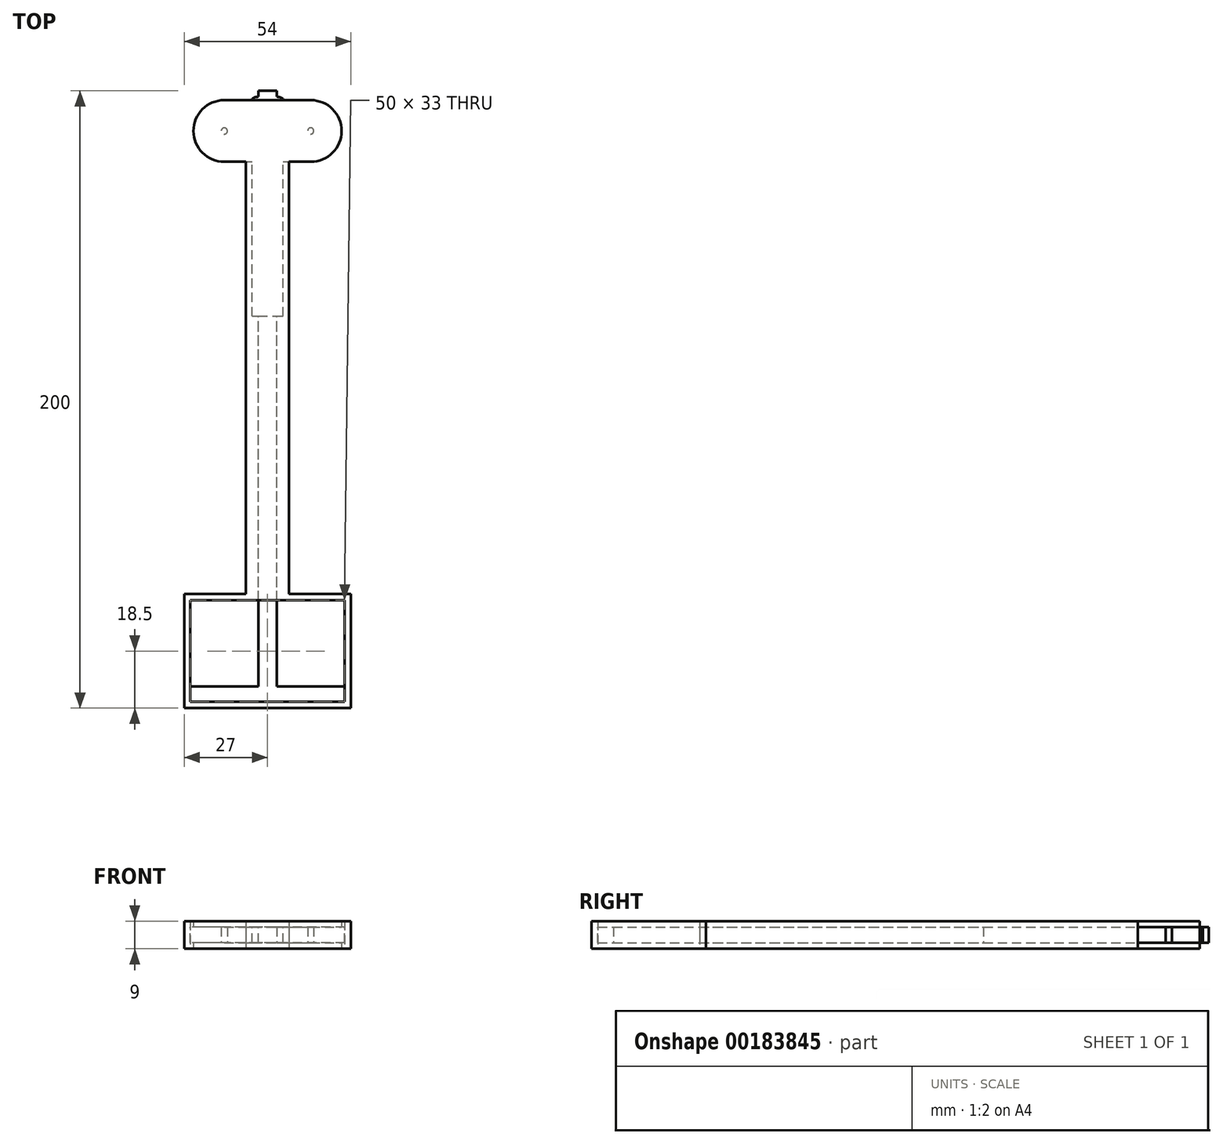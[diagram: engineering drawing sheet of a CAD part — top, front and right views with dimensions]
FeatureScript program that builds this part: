
annotation { "Feature Type Name" : "Feature", "Feature Type Description" : "" }
export const myFeature = defineFeature(function(context is Context, id is Id, definition is map)
    precondition{}
    {
        {
            var Q0;
            Q0=qCreatedBy(makeId("Top.planeOp"),FACE);
            var sketch = newSketch(context, id + "F0", { "sketchPlane" : qUnion([Q0])});
            skLineSegment(sketch, "E0.bottom", {"start": v(0, -180) * mm, "end": v(3, -180) * mm});
            skLineSegment(sketch, "E0.top", {"start": v(0, 13) * mm, "end": v(3, 13) * mm});
            skLineSegment(sketch, "E0.left", {"start": v(0, -180) * mm, "end": v(0, 13) * mm});
            skLineSegment(sketch, "E0.right", {"start": v(3, -180) * mm, "end": v(3, 13) * mm});
            skLineSegment(sketch, "E1", {"start": v(0, 10) * mm, "end": v(3, 10) * mm, "construction": true});
            skArc(sketch, "E2", {"start": v(3, 11.09) * mm, "mid": v(4.04, 10.94) * mm, "end": v(5, 10.5) * mm});
            skLineSegment(sketch, "E3", {"start": v(5, 10.5) * mm, "end": v(5, 10) * mm});
            skArc(sketch, "E4.MirrorCS", {"start": v(3, 8.91) * mm, "mid": v(4.04, 9.06) * mm, "end": v(5, 9.5) * mm});
            skLineSegment(sketch, "E5.MirrorCS", {"start": v(5, 9.5) * mm, "end": v(5, 10) * mm});
            skArc(sketch, "E6.1.0.0", {"start": v(3, 7.89) * mm, "mid": v(4.04, 7.74) * mm, "end": v(5, 7.3) * mm});
            skLineSegment(sketch, "E6.1.0.1", {"start": v(5, 7.3) * mm, "end": v(5, 6.8) * mm});
            skLineSegment(sketch, "E6.1.0.2", {"start": v(5, 6.3) * mm, "end": v(5, 6.8) * mm});
            skArc(sketch, "E6.1.0.3", {"start": v(3, 5.71) * mm, "mid": v(4.04, 5.86) * mm, "end": v(5, 6.3) * mm});
            skArc(sketch, "E6.2.0.0", {"start": v(3, 4.69) * mm, "mid": v(4.04, 4.54) * mm, "end": v(5, 4.1) * mm});
            skLineSegment(sketch, "E6.2.0.1", {"start": v(5, 4.1) * mm, "end": v(5, 3.6) * mm});
            skLineSegment(sketch, "E6.2.0.2", {"start": v(5, 3.1) * mm, "end": v(5, 3.6) * mm});
            skArc(sketch, "E6.2.0.3", {"start": v(3, 2.51) * mm, "mid": v(4.04, 2.66) * mm, "end": v(5, 3.1) * mm});
            skLineSegment(sketch, "E6.direction1", {"start": v(3, 7.39) * mm, "end": v(3, 4.19) * mm, "construction": true});
            skArc(sketch, "E7.0.3.0", {"start": v(3, 1.49) * mm, "mid": v(4.04, 1.34) * mm, "end": v(5, 0.9) * mm});
            skLineSegment(sketch, "E7.4.3.0", {"start": v(5, 0.9) * mm, "end": v(5, 0.4) * mm});
            skLineSegment(sketch, "E7.7.3.0", {"start": v(5, -0.1) * mm, "end": v(5, 0.4) * mm});
            skArc(sketch, "E7.10.3.0", {"start": v(3, -0.69) * mm, "mid": v(4.04, -0.54) * mm, "end": v(5, -0.1) * mm});
            skArc(sketch, "E7.0.4.0", {"start": v(3, -1.71) * mm, "mid": v(4.04, -1.86) * mm, "end": v(5, -2.3) * mm});
            skLineSegment(sketch, "E7.4.4.0", {"start": v(5, -2.3) * mm, "end": v(5, -2.8) * mm});
            skLineSegment(sketch, "E7.7.4.0", {"start": v(5, -3.3) * mm, "end": v(5, -2.8) * mm});
            skArc(sketch, "E7.10.4.0", {"start": v(3, -3.89) * mm, "mid": v(4.04, -3.74) * mm, "end": v(5, -3.3) * mm});
            skArc(sketch, "E7.0.5.0", {"start": v(3, -4.91) * mm, "mid": v(4.04, -5.06) * mm, "end": v(5, -5.5) * mm});
            skLineSegment(sketch, "E7.4.5.0", {"start": v(5, -5.5) * mm, "end": v(5, -6) * mm});
            skLineSegment(sketch, "E7.7.5.0", {"start": v(5, -6.5) * mm, "end": v(5, -6) * mm});
            skArc(sketch, "E7.10.5.0", {"start": v(3, -7.09) * mm, "mid": v(4.04, -6.94) * mm, "end": v(5, -6.5) * mm});
            skArc(sketch, "E7.0.6.0", {"start": v(3, -8.11) * mm, "mid": v(4.04, -8.26) * mm, "end": v(5, -8.7) * mm});
            skLineSegment(sketch, "E7.4.6.0", {"start": v(5, -8.7) * mm, "end": v(5, -9.2) * mm});
            skLineSegment(sketch, "E7.7.6.0", {"start": v(5, -9.7) * mm, "end": v(5, -9.2) * mm});
            skArc(sketch, "E7.10.6.0", {"start": v(3, -10.29) * mm, "mid": v(4.04, -10.14) * mm, "end": v(5, -9.7) * mm});
            skArc(sketch, "E7.0.7.0", {"start": v(3, -11.31) * mm, "mid": v(4.04, -11.46) * mm, "end": v(5, -11.9) * mm});
            skLineSegment(sketch, "E7.4.7.0", {"start": v(5, -11.9) * mm, "end": v(5, -12.4) * mm});
            skLineSegment(sketch, "E7.7.7.0", {"start": v(5, -12.9) * mm, "end": v(5, -12.4) * mm});
            skArc(sketch, "E7.10.7.0", {"start": v(3, -13.49) * mm, "mid": v(4.04, -13.34) * mm, "end": v(5, -12.9) * mm});
            skArc(sketch, "E7.0.8.0", {"start": v(3, -14.51) * mm, "mid": v(4.04, -14.66) * mm, "end": v(5, -15.1) * mm});
            skLineSegment(sketch, "E7.4.8.0", {"start": v(5, -15.1) * mm, "end": v(5, -15.6) * mm});
            skLineSegment(sketch, "E7.7.8.0", {"start": v(5, -16.1) * mm, "end": v(5, -15.6) * mm});
            skArc(sketch, "E7.10.8.0", {"start": v(3, -16.69) * mm, "mid": v(4.04, -16.54) * mm, "end": v(5, -16.1) * mm});
            skArc(sketch, "E7.0.9.0", {"start": v(3, -17.71) * mm, "mid": v(4.04, -17.86) * mm, "end": v(5, -18.3) * mm});
            skLineSegment(sketch, "E7.4.9.0", {"start": v(5, -18.3) * mm, "end": v(5, -18.8) * mm});
            skLineSegment(sketch, "E7.7.9.0", {"start": v(5, -19.3) * mm, "end": v(5, -18.8) * mm});
            skArc(sketch, "E7.10.9.0", {"start": v(3, -19.89) * mm, "mid": v(4.04, -19.74) * mm, "end": v(5, -19.3) * mm});
            skArc(sketch, "E7.0.10.0", {"start": v(3, -20.91) * mm, "mid": v(4.04, -21.06) * mm, "end": v(5, -21.5) * mm});
            skLineSegment(sketch, "E7.4.10.0", {"start": v(5, -21.5) * mm, "end": v(5, -22) * mm});
            skLineSegment(sketch, "E7.7.10.0", {"start": v(5, -22.5) * mm, "end": v(5, -22) * mm});
            skArc(sketch, "E7.10.10.0", {"start": v(3, -23.09) * mm, "mid": v(4.04, -22.94) * mm, "end": v(5, -22.5) * mm});
            skArc(sketch, "E7.0.11.0", {"start": v(3, -24.11) * mm, "mid": v(4.04, -24.26) * mm, "end": v(5, -24.7) * mm});
            skLineSegment(sketch, "E7.4.11.0", {"start": v(5, -24.7) * mm, "end": v(5, -25.2) * mm});
            skLineSegment(sketch, "E7.7.11.0", {"start": v(5, -25.7) * mm, "end": v(5, -25.2) * mm});
            skArc(sketch, "E7.10.11.0", {"start": v(3, -26.29) * mm, "mid": v(4.04, -26.14) * mm, "end": v(5, -25.7) * mm});
            skArc(sketch, "E7.0.12.0", {"start": v(3, -27.31) * mm, "mid": v(4.04, -27.46) * mm, "end": v(5, -27.9) * mm});
            skLineSegment(sketch, "E7.4.12.0", {"start": v(5, -27.9) * mm, "end": v(5, -28.4) * mm});
            skLineSegment(sketch, "E7.7.12.0", {"start": v(5, -28.9) * mm, "end": v(5, -28.4) * mm});
            skArc(sketch, "E7.10.12.0", {"start": v(3, -29.49) * mm, "mid": v(4.04, -29.34) * mm, "end": v(5, -28.9) * mm});
            skArc(sketch, "E7.0.13.0", {"start": v(3, -30.51) * mm, "mid": v(4.04, -30.66) * mm, "end": v(5, -31.1) * mm});
            skLineSegment(sketch, "E7.4.13.0", {"start": v(5, -31.1) * mm, "end": v(5, -31.6) * mm});
            skLineSegment(sketch, "E7.7.13.0", {"start": v(5, -32.1) * mm, "end": v(5, -31.6) * mm});
            skArc(sketch, "E7.10.13.0", {"start": v(3, -32.69) * mm, "mid": v(4.04, -32.54) * mm, "end": v(5, -32.1) * mm});
            skArc(sketch, "E7.0.14.0", {"start": v(3, -33.71) * mm, "mid": v(4.04, -33.86) * mm, "end": v(5, -34.3) * mm});
            skLineSegment(sketch, "E7.4.14.0", {"start": v(5, -34.3) * mm, "end": v(5, -34.8) * mm});
            skLineSegment(sketch, "E7.7.14.0", {"start": v(5, -35.3) * mm, "end": v(5, -34.8) * mm});
            skArc(sketch, "E7.10.14.0", {"start": v(3, -35.89) * mm, "mid": v(4.04, -35.74) * mm, "end": v(5, -35.3) * mm});
            skArc(sketch, "E7.0.15.0", {"start": v(3, -36.91) * mm, "mid": v(4.04, -37.06) * mm, "end": v(5, -37.5) * mm});
            skLineSegment(sketch, "E7.4.15.0", {"start": v(5, -37.5) * mm, "end": v(5, -38) * mm});
            skLineSegment(sketch, "E7.7.15.0", {"start": v(5, -38.5) * mm, "end": v(5, -38) * mm});
            skArc(sketch, "E7.10.15.0", {"start": v(3, -39.09) * mm, "mid": v(4.04, -38.94) * mm, "end": v(5, -38.5) * mm});
            skSolve(sketch);
        }
        {
            var Q0;
            Q0 = qSketchRegion(id + "F0", true);
            extrude(context, id + "F1", {"entities" : qUnion([Q0]), "depth" : 5 * mm});
        }
        {
            var Q0;
            Q0=makeQuery(id+"F1.opExtrude","SWEPT_BODY",BODY,{"disambiguationData":[OSD([sQuery(id+"F0.wireOp",EDGE,"E0.bottom"),sQuery(id+"F0.wireOp",EDGE,"E0.top"),sQuery(id+"F0.wireOp",EDGE,"E0.left"),sQuery(id+"F0.wireOp",EDGE,"E0.right"),sQuery(id+"F0.wireOp",EDGE,"E2"),sQuery(id+"F0.wireOp",EDGE,"E3"),sQuery(id+"F0.wireOp",EDGE,"E4.MirrorCS"),sQuery(id+"F0.wireOp",EDGE,"E5.MirrorCS"),sQuery(id+"F0.wireOp",EDGE,"E6.1.0.0"),sQuery(id+"F0.wireOp",EDGE,"E6.1.0.1"),sQuery(id+"F0.wireOp",EDGE,"E6.1.0.2"),sQuery(id+"F0.wireOp",EDGE,"E6.1.0.3"),sQuery(id+"F0.wireOp",EDGE,"E6.2.0.0"),sQuery(id+"F0.wireOp",EDGE,"E6.2.0.1"),sQuery(id+"F0.wireOp",EDGE,"E6.2.0.2"),sQuery(id+"F0.wireOp",EDGE,"E6.2.0.3"),sQuery(id+"F0.wireOp",EDGE,"E7.0.3.0"),sQuery(id+"F0.wireOp",EDGE,"E7.4.3.0"),sQuery(id+"F0.wireOp",EDGE,"E7.7.3.0"),sQuery(id+"F0.wireOp",EDGE,"E7.10.3.0"),sQuery(id+"F0.wireOp",EDGE,"E7.0.4.0"),sQuery(id+"F0.wireOp",EDGE,"E7.4.4.0"),sQuery(id+"F0.wireOp",EDGE,"E7.7.4.0"),sQuery(id+"F0.wireOp",EDGE,"E7.10.4.0"),sQuery(id+"F0.wireOp",EDGE,"E7.0.5.0"),sQuery(id+"F0.wireOp",EDGE,"E7.4.5.0"),sQuery(id+"F0.wireOp",EDGE,"E7.7.5.0"),sQuery(id+"F0.wireOp",EDGE,"E7.10.5.0"),sQuery(id+"F0.wireOp",EDGE,"E7.0.6.0"),sQuery(id+"F0.wireOp",EDGE,"E7.4.6.0"),sQuery(id+"F0.wireOp",EDGE,"E7.7.6.0"),sQuery(id+"F0.wireOp",EDGE,"E7.10.6.0"),sQuery(id+"F0.wireOp",EDGE,"E7.0.7.0"),sQuery(id+"F0.wireOp",EDGE,"E7.4.7.0"),sQuery(id+"F0.wireOp",EDGE,"E7.7.7.0"),sQuery(id+"F0.wireOp",EDGE,"E7.10.7.0"),sQuery(id+"F0.wireOp",EDGE,"E7.0.8.0"),sQuery(id+"F0.wireOp",EDGE,"E7.4.8.0"),sQuery(id+"F0.wireOp",EDGE,"E7.7.8.0"),sQuery(id+"F0.wireOp",EDGE,"E7.10.8.0"),sQuery(id+"F0.wireOp",EDGE,"E7.0.9.0"),sQuery(id+"F0.wireOp",EDGE,"E7.4.9.0"),sQuery(id+"F0.wireOp",EDGE,"E7.7.9.0"),sQuery(id+"F0.wireOp",EDGE,"E7.10.9.0"),sQuery(id+"F0.wireOp",EDGE,"E7.0.10.0"),sQuery(id+"F0.wireOp",EDGE,"E7.4.10.0"),sQuery(id+"F0.wireOp",EDGE,"E7.7.10.0"),sQuery(id+"F0.wireOp",EDGE,"E7.10.10.0"),sQuery(id+"F0.wireOp",EDGE,"E7.0.11.0"),sQuery(id+"F0.wireOp",EDGE,"E7.4.11.0"),sQuery(id+"F0.wireOp",EDGE,"E7.7.11.0"),sQuery(id+"F0.wireOp",EDGE,"E7.10.11.0"),sQuery(id+"F0.wireOp",EDGE,"E7.0.12.0"),sQuery(id+"F0.wireOp",EDGE,"E7.4.12.0"),sQuery(id+"F0.wireOp",EDGE,"E7.7.12.0"),sQuery(id+"F0.wireOp",EDGE,"E7.10.12.0"),sQuery(id+"F0.wireOp",EDGE,"E7.0.13.0"),sQuery(id+"F0.wireOp",EDGE,"E7.4.13.0"),sQuery(id+"F0.wireOp",EDGE,"E7.7.13.0"),sQuery(id+"F0.wireOp",EDGE,"E7.10.13.0"),sQuery(id+"F0.wireOp",EDGE,"E7.0.14.0"),sQuery(id+"F0.wireOp",EDGE,"E7.4.14.0"),sQuery(id+"F0.wireOp",EDGE,"E7.7.14.0"),sQuery(id+"F0.wireOp",EDGE,"E7.10.14.0"),sQuery(id+"F0.wireOp",EDGE,"E7.0.15.0"),sQuery(id+"F0.wireOp",EDGE,"E7.4.15.0"),sQuery(id+"F0.wireOp",EDGE,"E7.7.15.0"),sQuery(id+"F0.wireOp",EDGE,"E7.10.15.0")])]});
            var Q1;
            Q1=makeQuery(id+"F1.opExtrude","SWEPT_FACE",FACE,{"disambiguationData":[OSD([sQuery(id+"F0.wireOp",EDGE,"E0.left")])]});
            mirror(context, id + "F2", {"operationType" : NewBodyOperationType.ADD, "entities" : qUnion([Q0]), "mirrorPlane" : qUnion([Q1])});
        }
        {
            var Q0;
            {var subQ0=makeQuery(id+"F1.opExtrude","SWEPT_FACE",FACE,{"disambiguationData":[OSD([sQuery(id+"F0.wireOp",EDGE,"E0.bottom")])]});Q0=makeQuery(id+"F2.boolean.opBoolean","MERGE",FACE,{"derivedFrom":[subQ0,makeQuery(id+"F2.opPattern","COPY",FACE,{"derivedFrom":subQ0,"instanceName":"1"})]});}
            var sketch = newSketch(context, id + "F3", { "sketchPlane" : qUnion([Q0])});
            skLineSegment(sketch, "E8.bottom", {"start": v(25, 0) * mm, "end": v(-25, 0) * mm});
            skLineSegment(sketch, "E8.top", {"start": v(25, 5) * mm, "end": v(-25, 5) * mm});
            skLineSegment(sketch, "E8.left", {"start": v(25, 0) * mm, "end": v(25, 5) * mm});
            skLineSegment(sketch, "E8.right", {"start": v(-25, 0) * mm, "end": v(-25, 5) * mm});
            skPoint(sketch, "E8.middle", {"position": v(0, 2.5) * mm});
            skPoint(sketch, "E8.middle.positionSnap0", {"position": v(-3, 2.5) * mm});
            skPoint(sketch, "E8.middle.positionSnap1", {"position": v(0, 0) * mm});
            skPoint(sketch, "E8.centerSnap0", {"position": v(-3, 2.5) * mm});
            skPoint(sketch, "E8.centerSnap1", {"position": v(0, 0) * mm});
            skSolve(sketch);
        }
        {
            var Q0;
            Q0 = qSketchRegion(id + "F3", true);
            extrude(context, id + "F4", {"entities" : qUnion([Q0]), "operationType" : NewBodyOperationType.ADD, "depth" : 5 * mm});
        }
        {
            var Q0;
            Q0=qCreatedBy(makeId("Top.planeOp"),FACE);
            var sketch = newSketch(context, id + "F5", { "sketchPlane" : qUnion([Q0])});
            skCircle(sketch, "E9", {"center": v(14, 0) * mm, "radius": 10 * mm});
            skLineSegment(sketch, "E10", {"start": v(7, -10) * mm, "end": v(7, -150) * mm});
            skLineSegment(sketch, "E11", {"start": v(7, -150) * mm, "end": v(27, -150) * mm});
            skLineSegment(sketch, "E12", {"start": v(27, -150) * mm, "end": v(27, -187) * mm});
            skLineSegment(sketch, "E13", {"start": v(27, -187) * mm, "end": v(0, -187) * mm});
            skLineSegment(sketch, "E14", {"start": v(0, 10) * mm, "end": v(14, 10) * mm});
            skLineSegment(sketch, "E15", {"start": v(7, -10) * mm, "end": v(14, -10) * mm});
            skLineSegment(sketch, "E16.MirrorCS", {"start": v(0, 10) * mm, "end": v(-14, 10) * mm});
            skLineSegment(sketch, "E17.MirrorCS", {"start": v(-7, -10) * mm, "end": v(-14, -10) * mm});
            skCircle(sketch, "E18.MirrorC", {"center": v(-14, 0) * mm, "radius": 10 * mm});
            skLineSegment(sketch, "E19.MirrorCS", {"start": v(-7, -10) * mm, "end": v(-7, -150) * mm});
            skLineSegment(sketch, "E20.MirrorCS", {"start": v(-7, -150) * mm, "end": v(-27, -150) * mm});
            skLineSegment(sketch, "E21.MirrorCS", {"start": v(-27, -150) * mm, "end": v(-27, -187) * mm});
            skLineSegment(sketch, "E22.MirrorCS", {"start": v(-27, -187) * mm, "end": v(0, -187) * mm});
            skLineSegment(sketch, "E23.bottom", {"start": v(25, -185) * mm, "end": v(-25, -185) * mm});
            skLineSegment(sketch, "E23.top", {"start": v(25, -152) * mm, "end": v(-25, -152) * mm});
            skLineSegment(sketch, "E23.left", {"start": v(25, -185) * mm, "end": v(25, -152) * mm});
            skLineSegment(sketch, "E23.right", {"start": v(-25, -185) * mm, "end": v(-25, -152) * mm});
            skPoint(sketch, "E23.middle", {"position": v(0, -168.5) * mm});
            skSolve(sketch);
        }
        {
            var Q0;
            Q0 = qSketchRegion(id + "F5", true);
            extrude(context, id + "F6", {"entities" : qUnion([Q0]), "depth" : 7 * mm, "hasSecondDirection" : true, "secondDirectionOppositeDirection" : true, "secondDirectionDepth" : 2 * mm});
        }
        {
            var Q0;
            Q0=makeQuery(id+"F1.opExtrude","SWEPT_BODY",BODY,{"disambiguationData":[OSD([sQuery(id+"F0.wireOp",EDGE,"E0.bottom"),sQuery(id+"F0.wireOp",EDGE,"E0.top"),sQuery(id+"F0.wireOp",EDGE,"E0.left"),sQuery(id+"F0.wireOp",EDGE,"E0.right"),sQuery(id+"F0.wireOp",EDGE,"E2"),sQuery(id+"F0.wireOp",EDGE,"E3"),sQuery(id+"F0.wireOp",EDGE,"E4.MirrorCS"),sQuery(id+"F0.wireOp",EDGE,"E5.MirrorCS"),sQuery(id+"F0.wireOp",EDGE,"E6.1.0.0"),sQuery(id+"F0.wireOp",EDGE,"E6.1.0.1"),sQuery(id+"F0.wireOp",EDGE,"E6.1.0.2"),sQuery(id+"F0.wireOp",EDGE,"E6.1.0.3"),sQuery(id+"F0.wireOp",EDGE,"E6.2.0.0"),sQuery(id+"F0.wireOp",EDGE,"E6.2.0.1"),sQuery(id+"F0.wireOp",EDGE,"E6.2.0.2"),sQuery(id+"F0.wireOp",EDGE,"E6.2.0.3"),sQuery(id+"F0.wireOp",EDGE,"E7.0.3.0"),sQuery(id+"F0.wireOp",EDGE,"E7.4.3.0"),sQuery(id+"F0.wireOp",EDGE,"E7.7.3.0"),sQuery(id+"F0.wireOp",EDGE,"E7.10.3.0"),sQuery(id+"F0.wireOp",EDGE,"E7.0.4.0"),sQuery(id+"F0.wireOp",EDGE,"E7.4.4.0"),sQuery(id+"F0.wireOp",EDGE,"E7.7.4.0"),sQuery(id+"F0.wireOp",EDGE,"E7.10.4.0"),sQuery(id+"F0.wireOp",EDGE,"E7.0.5.0"),sQuery(id+"F0.wireOp",EDGE,"E7.4.5.0"),sQuery(id+"F0.wireOp",EDGE,"E7.7.5.0"),sQuery(id+"F0.wireOp",EDGE,"E7.10.5.0"),sQuery(id+"F0.wireOp",EDGE,"E7.0.6.0"),sQuery(id+"F0.wireOp",EDGE,"E7.4.6.0"),sQuery(id+"F0.wireOp",EDGE,"E7.7.6.0"),sQuery(id+"F0.wireOp",EDGE,"E7.10.6.0"),sQuery(id+"F0.wireOp",EDGE,"E7.0.7.0"),sQuery(id+"F0.wireOp",EDGE,"E7.4.7.0"),sQuery(id+"F0.wireOp",EDGE,"E7.7.7.0"),sQuery(id+"F0.wireOp",EDGE,"E7.10.7.0"),sQuery(id+"F0.wireOp",EDGE,"E7.0.8.0"),sQuery(id+"F0.wireOp",EDGE,"E7.4.8.0"),sQuery(id+"F0.wireOp",EDGE,"E7.7.8.0"),sQuery(id+"F0.wireOp",EDGE,"E7.10.8.0"),sQuery(id+"F0.wireOp",EDGE,"E7.0.9.0"),sQuery(id+"F0.wireOp",EDGE,"E7.4.9.0"),sQuery(id+"F0.wireOp",EDGE,"E7.7.9.0"),sQuery(id+"F0.wireOp",EDGE,"E7.10.9.0"),sQuery(id+"F0.wireOp",EDGE,"E7.0.10.0"),sQuery(id+"F0.wireOp",EDGE,"E7.4.10.0"),sQuery(id+"F0.wireOp",EDGE,"E7.7.10.0"),sQuery(id+"F0.wireOp",EDGE,"E7.10.10.0"),sQuery(id+"F0.wireOp",EDGE,"E7.0.11.0"),sQuery(id+"F0.wireOp",EDGE,"E7.4.11.0"),sQuery(id+"F0.wireOp",EDGE,"E7.7.11.0"),sQuery(id+"F0.wireOp",EDGE,"E7.10.11.0"),sQuery(id+"F0.wireOp",EDGE,"E7.0.12.0"),sQuery(id+"F0.wireOp",EDGE,"E7.4.12.0"),sQuery(id+"F0.wireOp",EDGE,"E7.7.12.0"),sQuery(id+"F0.wireOp",EDGE,"E7.10.12.0"),sQuery(id+"F0.wireOp",EDGE,"E7.0.13.0"),sQuery(id+"F0.wireOp",EDGE,"E7.4.13.0"),sQuery(id+"F0.wireOp",EDGE,"E7.7.13.0"),sQuery(id+"F0.wireOp",EDGE,"E7.10.13.0"),sQuery(id+"F0.wireOp",EDGE,"E7.0.14.0"),sQuery(id+"F0.wireOp",EDGE,"E7.4.14.0"),sQuery(id+"F0.wireOp",EDGE,"E7.7.14.0"),sQuery(id+"F0.wireOp",EDGE,"E7.10.14.0"),sQuery(id+"F0.wireOp",EDGE,"E7.0.15.0"),sQuery(id+"F0.wireOp",EDGE,"E7.4.15.0"),sQuery(id+"F0.wireOp",EDGE,"E7.7.15.0"),sQuery(id+"F0.wireOp",EDGE,"E7.10.15.0")])]});
            var Q1;
            Q1=makeQuery(id+"F6.opExtrude","SWEPT_BODY",BODY,{"disambiguationData":[OSD([sQuery(id+"F5.wireOp",EDGE,"E9"),sQuery(id+"F5.wireOp",EDGE,"E10"),sQuery(id+"F5.wireOp",EDGE,"E11"),sQuery(id+"F5.wireOp",EDGE,"E12"),sQuery(id+"F5.wireOp",EDGE,"E13"),sQuery(id+"F5.wireOp",EDGE,"E14"),sQuery(id+"F5.wireOp",EDGE,"E15"),sQuery(id+"F5.wireOp",EDGE,"E16.MirrorCS"),sQuery(id+"F5.wireOp",EDGE,"E17.MirrorCS"),sQuery(id+"F5.wireOp",EDGE,"E18.MirrorC"),sQuery(id+"F5.wireOp",EDGE,"E19.MirrorCS"),sQuery(id+"F5.wireOp",EDGE,"E20.MirrorCS"),sQuery(id+"F5.wireOp",EDGE,"E21.MirrorCS"),sQuery(id+"F5.wireOp",EDGE,"E22.MirrorCS"),sQuery(id+"F5.wireOp",EDGE,"E23.bottom"),sQuery(id+"F5.wireOp",EDGE,"E23.top"),sQuery(id+"F5.wireOp",EDGE,"E23.left"),sQuery(id+"F5.wireOp",EDGE,"E23.right")])]});
            booleanBodies(context, id + "F7", {"operationType" : BooleanOperationType.SUBTRACTION, "tools" : qUnion([Q0]), "targets" : qUnion([Q1]), "keepTools" : true});
        }
        {
            var Q0;
            Q0=qCreatedBy(makeId("Top.planeOp"),FACE);
            var sketch = newSketch(context, id + "F8", { "sketchPlane" : qUnion([Q0])});
            skArc(sketch, "E24.0", {"start": v(-14, -10) * mm, "mid": v(-24, 0) * mm, "end": v(-14, 10) * mm});
            skLineSegment(sketch, "E25.0", {"start": v(-14, 10) * mm, "end": v(14, 10) * mm});
            skArc(sketch, "E26.0", {"start": v(14, -10) * mm, "mid": v(24, 0) * mm, "end": v(14, 10) * mm});
            skLineSegment(sketch, "E27", {"start": v(-14, -10) * mm, "end": v(14, -10) * mm});
            skSolve(sketch);
        }
        {
            var Q0;
            Q0 = qSketchRegion(id + "F8", true);
            extrude(context, id + "F9", {"entities" : qUnion([Q0]), "operationType" : NewBodyOperationType.REMOVE, "depth" : 5 * mm});
        }
        {
            var Q0;
            {var subQ70=sQuery(id+"F8.wireOp",EDGE,"E27");Q0=makeQuery(id+"F9.boolean.opBoolean","COPY",FACE,{"disambiguationData":[TD([makeQuery(id+"F6.opExtrude","SWEPT_FACE",FACE,{"disambiguationData":[OSD([sQuery(id+"F5.wireOp",EDGE,"E17.MirrorCS")])]})])],"derivedFrom":makeQuery(id+"F9.opExtrude","SWEPT_FACE",FACE,{"disambiguationData":[OSD([subQ70])]})});}
            var sketch = newSketch(context, id + "F10", { "sketchPlane" : qUnion([Q0])});
            skLineSegment(sketch, "E28.bottom", {"start": v(5, 0) * mm, "end": v(-5, 0) * mm});
            skLineSegment(sketch, "E28.top", {"start": v(5, 5) * mm, "end": v(-5, 5) * mm});
            skLineSegment(sketch, "E28.left", {"start": v(5, 0) * mm, "end": v(5, 5) * mm});
            skLineSegment(sketch, "E28.right", {"start": v(-5, 0) * mm, "end": v(-5, 5) * mm});
            skPoint(sketch, "E28.middle", {"position": v(0, 2.5) * mm});
            skSolve(sketch);
        }
        {
            var Q0;
            Q0 = qSketchRegion(id + "F10", true);
            extrude(context, id + "F11", {"entities" : qUnion([Q0]), "operationType" : NewBodyOperationType.REMOVE, "oppositeDirection" : true, "depth" : 50 * mm});
        }
        {
            var Q0;
            Q0=qCreatedBy(makeId("Top.planeOp"),FACE);
            var sketch = newSketch(context, id + "F12", { "sketchPlane" : qUnion([Q0])});
            skCircle(sketch, "E29", {"center": v(-14, 0) * mm, "radius": 1 * mm});
            skCircle(sketch, "E30", {"center": v(14, 0) * mm, "radius": 1 * mm});
            skSolve(sketch);
        }
        {
            var Q0;
            Q0 = qSketchRegion(id + "F12", true);
            extrude(context, id + "F13", {"entities" : qUnion([Q0]), "operationType" : NewBodyOperationType.ADD, "endBound" : BoundingType.UP_TO_NEXT, "depth" : 25 * mm});
        }
    });
